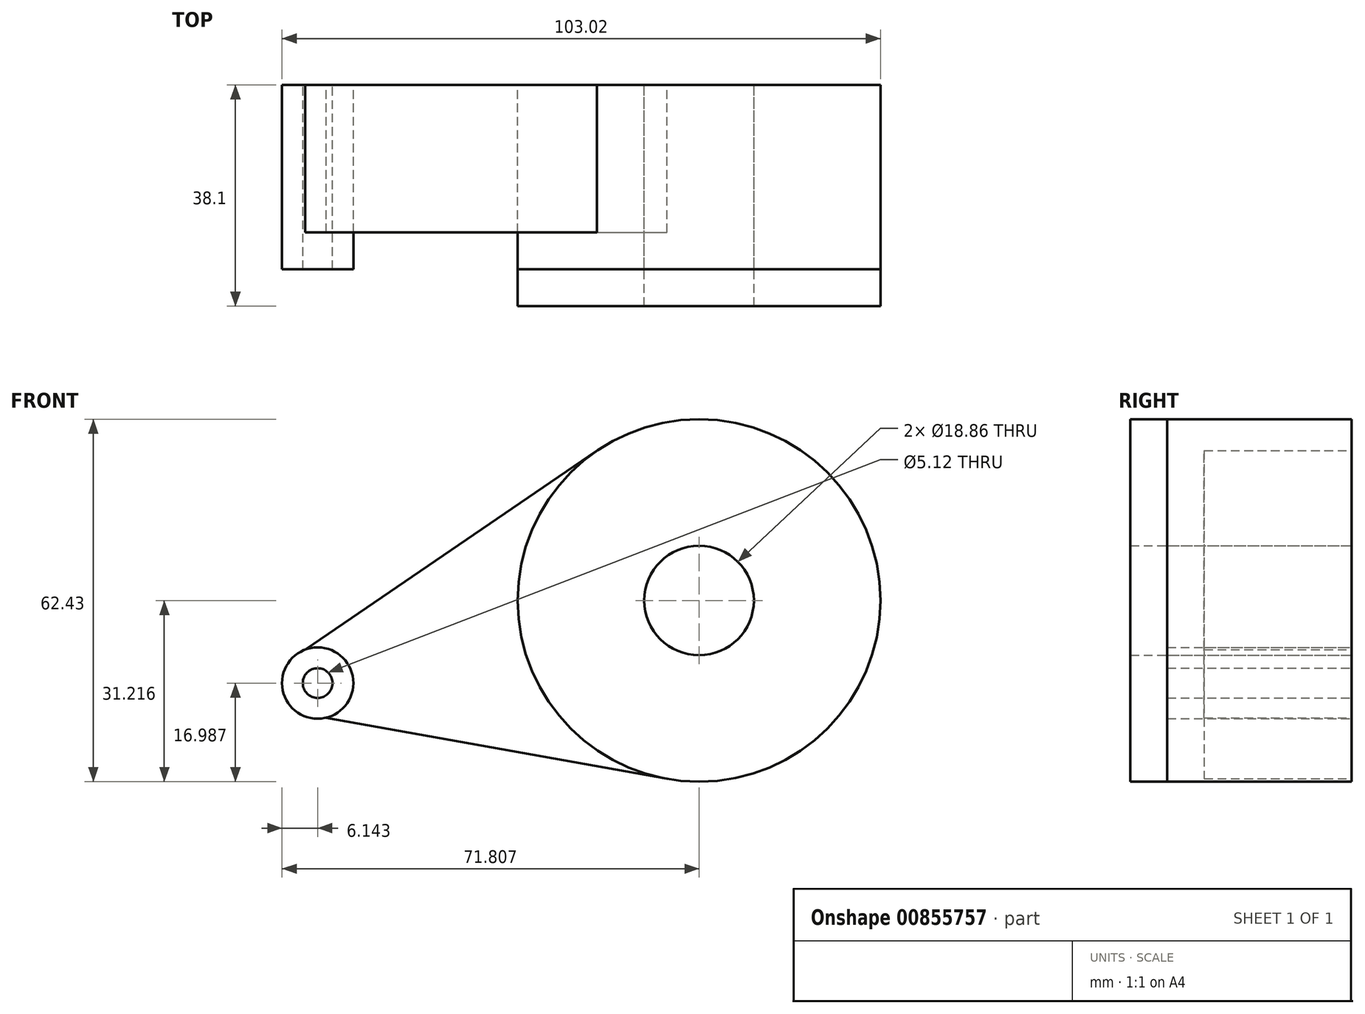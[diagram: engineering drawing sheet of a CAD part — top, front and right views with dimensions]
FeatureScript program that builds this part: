
annotation { "Feature Type Name" : "Feature", "Feature Type Description" : "" }
export const myFeature = defineFeature(function(context is Context, id is Id, definition is map)
    precondition{}
    {
        {
            var Q0;
            Q0=qCreatedBy(makeId("Front.planeOp"),FACE);
            var sketch = newSketch(context, id + "F0", { "sketchPlane" : qUnion([Q0])});
            skCircle(sketch, "E0", {"center": v(-42.52, 10.05) * mm, "radius": 6.15 * mm});
            skCircle(sketch, "E1", {"center": v(23.15, 24.28) * mm, "radius": 31.22 * mm});
            skLineSegment(sketch, "E2", {"start": v(-41.03, 4.08) * mm, "end": v(17.63, -6.45) * mm});
            skLineSegment(sketch, "E3", {"start": v(-44.66, 15.8) * mm, "end": v(5.55, 50.06) * mm});
            skCircle(sketch, "E4", {"center": v(-42.52, 10.05) * mm, "radius": 2.56 * mm});
            skCircle(sketch, "E5", {"center": v(23.15, 24.28) * mm, "radius": 9.43 * mm});
            skSolve(sketch);
        }
        {
            var Q0;
            Q0=makeQuery(id+"F0.imprint","IMPRINT",FACE,{"disambiguationData":[TD([[makeQuery(id+"F0.imprint","IMPRINT",EDGE,{"derivedFrom":sQuery(id+"F0.wireOp",EDGE,"E4")}),-1.0]])]});
            var Q1;
            Q1=makeQuery(id+"F0.imprint","IMPRINT",FACE,{"disambiguationData":[TD([[makeQuery(id+"F0.imprint","IMPRINT",EDGE,{"derivedFrom":sQuery(id+"F0.wireOp",EDGE,"E5")}),-1.0]])]});
            extrude(context, id + "F1", {"entities" : qUnion([Q0, Q1]), "depth" : 31.75 * mm, "offsetDistance" : 25.4 * mm});
        }
        {
            var Q0;
            {var subQ0=sQuery(id+"F0.wireOp",EDGE,"E2");Q0=makeQuery(id+"F0.imprint","IMPRINT",FACE,{"disambiguationData":[TD([[makeQuery(id+"F0.imprint","IMPRINT",EDGE,{"derivedFrom":subQ0}),1.0]])]});}
            extrude(context, id + "F2", {"entities" : qUnion([Q0]), "depth" : 25.4 * mm, "offsetDistance" : 25.4 * mm});
        }
        {
            var Q0;
            Q0=makeQuery(id+"F0.imprint","IMPRINT",FACE,{"disambiguationData":[TD([[makeQuery(id+"F0.imprint","IMPRINT",EDGE,{"derivedFrom":sQuery(id+"F0.wireOp",EDGE,"E5")}),-1.0]])]});
            extrude(context, id + "F3", {"entities" : qUnion([Q0]), "depth" : 38.1 * mm, "offsetDistance" : 25.4 * mm});
        }
    });
